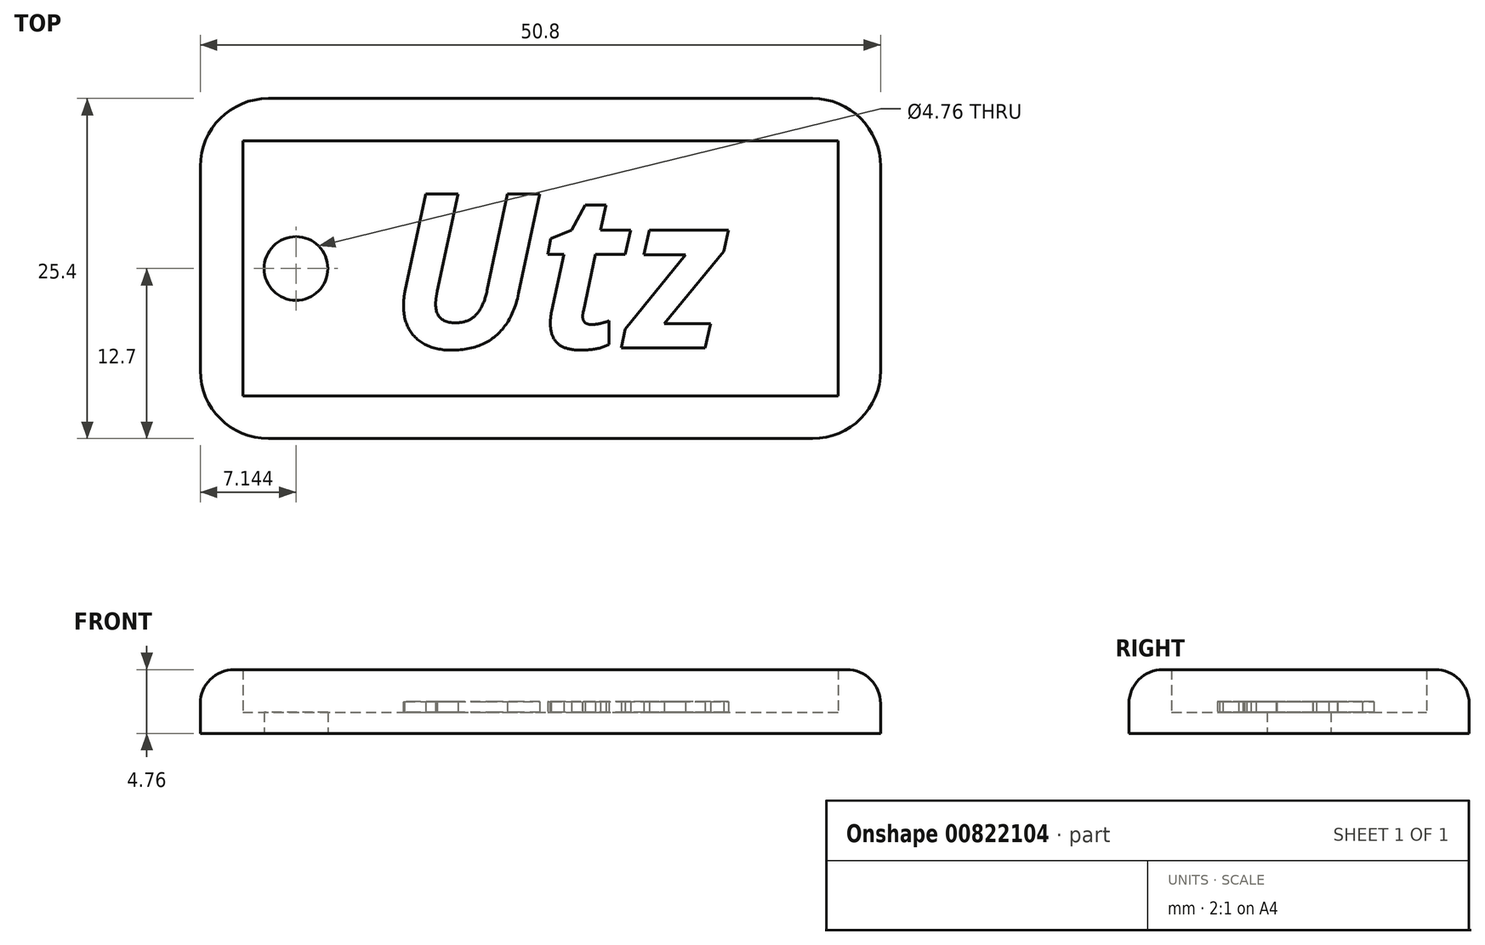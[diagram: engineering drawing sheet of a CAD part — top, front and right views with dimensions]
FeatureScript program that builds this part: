
annotation { "Feature Type Name" : "Feature", "Feature Type Description" : "" }
export const myFeature = defineFeature(function(context is Context, id is Id, definition is map)
    precondition{}
    {
        {
            var Q0;
            Q0=qCreatedBy(makeId("Top.planeOp"),FACE);
            var sketch = newSketch(context, id + "F0", { "sketchPlane" : qUnion([Q0])});
            skLineSegment(sketch, "E0.bottom", {"start": v(0, 0) * mm, "end": v(50.8, 0) * mm});
            skLineSegment(sketch, "E0.top", {"start": v(0, 25.4) * mm, "end": v(50.8, 25.4) * mm});
            skLineSegment(sketch, "E0.left", {"start": v(0, 0) * mm, "end": v(0, 25.4) * mm});
            skLineSegment(sketch, "E0.right", {"start": v(50.8, 0) * mm, "end": v(50.8, 25.4) * mm});
            skCircle(sketch, "E1", {"center": v(7.14, 12.7) * mm, "radius": 2.38 * mm});
            skPoint(sketch, "E1.centerSnap0", {"position": v(0, 12.7) * mm});
            skLineSegment(sketch, "E2.0", {"start": v(3.18, 22.23) * mm, "end": v(47.62, 22.23) * mm});
            skLineSegment(sketch, "E2.1", {"start": v(3.18, 3.18) * mm, "end": v(3.18, 22.22) * mm});
            skLineSegment(sketch, "E2.2", {"start": v(3.18, 3.18) * mm, "end": v(47.62, 3.18) * mm});
            skLineSegment(sketch, "E2.3", {"start": v(47.62, 3.18) * mm, "end": v(47.62, 22.23) * mm});
            skSolve(sketch);
        }
        {
            var Q0;
            Q0=makeQuery(id+"F0.imprint","IMPRINT",FACE,{"disambiguationData":[TD([[makeQuery(id+"F0.imprint","IMPRINT",EDGE,{"derivedFrom":sQuery(id+"F0.wireOp",EDGE,"E1")}),-1.0]])]});
            extrude(context, id + "F1", {"entities" : qUnion([Q0]), "depth" : 1.59 * mm, "offsetDistance" : 25.4 * mm});
        }
        {
            var Q0;
            Q0 = qSketchRegion(id + "F0", true);
            extrude(context, id + "F2", {"entities" : qUnion([Q0]), "operationType" : NewBodyOperationType.ADD, "depth" : 4.76 * mm, "offsetDistance" : 25.4 * mm});
        }
        {
            var Q0;
            Q0=makeQuery(id+"F2.opExtrude","SWEPT_EDGE",EDGE,{"disambiguationData":[OSD([sQuery(id+"F0.wireOp",EDGE,"E0.bottom"),sQuery(id+"F0.wireOp",EDGE,"E0.left")])]});
            var Q1;
            Q1=makeQuery(id+"F2.opExtrude","SWEPT_EDGE",EDGE,{"disambiguationData":[OSD([sQuery(id+"F0.wireOp",EDGE,"E0.bottom"),sQuery(id+"F0.wireOp",EDGE,"E0.right")])]});
            var Q2;
            Q2=makeQuery(id+"F2.opExtrude","SWEPT_EDGE",EDGE,{"disambiguationData":[OSD([sQuery(id+"F0.wireOp",EDGE,"E0.top"),sQuery(id+"F0.wireOp",EDGE,"E0.right")])]});
            var Q3;
            Q3=makeQuery(id+"F2.opExtrude","SWEPT_EDGE",EDGE,{"disambiguationData":[OSD([sQuery(id+"F0.wireOp",EDGE,"E0.top"),sQuery(id+"F0.wireOp",EDGE,"E0.left")])]});
            fillet(context, id + "F3", {"entities" : qUnion([Q0, Q1, Q2, Q3]), "radius" : 5.08 * mm, "tangentPropagation" : true, "allowEdgeOverflow" : false});
        }
        {
            var Q0;
            Q0=makeQuery(id+"F2.opExtrude","CAP_EDGE",EDGE,{"disambiguationData":[OSD([sQuery(id+"F0.wireOp",EDGE,"E0.top")])],"isStart":false});
            fillet(context, id + "F4", {"entities" : qUnion([Q0]), "radius" : 2.54 * mm, "tangentPropagation" : true, "allowEdgeOverflow" : false});
        }
        {
            var Q0;
            Q0=makeQuery(id+"F1.opExtrude","CAP_FACE",FACE,{"disambiguationData":[OSD([sQuery(id+"F0.wireOp",EDGE,"E1"),sQuery(id+"F0.wireOp",EDGE,"E2.0"),sQuery(id+"F0.wireOp",EDGE,"E2.1"),sQuery(id+"F0.wireOp",EDGE,"E2.2"),sQuery(id+"F0.wireOp",EDGE,"E2.3")])],"isStart":false});
            var sketch = newSketch(context, id + "F5", { "sketchPlane" : qUnion([Q0])});
            skText(sketch, "E3", { "text": "Utz", "fontName": "OpenSans-BoldItalic.ttf"});
            const initialGuessF5  = {"E3": [0.01406, 0.00676, 1, 0, 0.01161]};
            skSetInitialGuess(sketch, initialGuessF5);
            skSolve(sketch);
        }
        {
            var Q0;
            Q0 = qSketchRegion(id + "F5", true);
            extrude(context, id + "F6", {"entities" : qUnion([Q0]), "operationType" : NewBodyOperationType.ADD, "depth" : 0.8 * mm, "offsetDistance" : 25.4 * mm});
        }
    });
